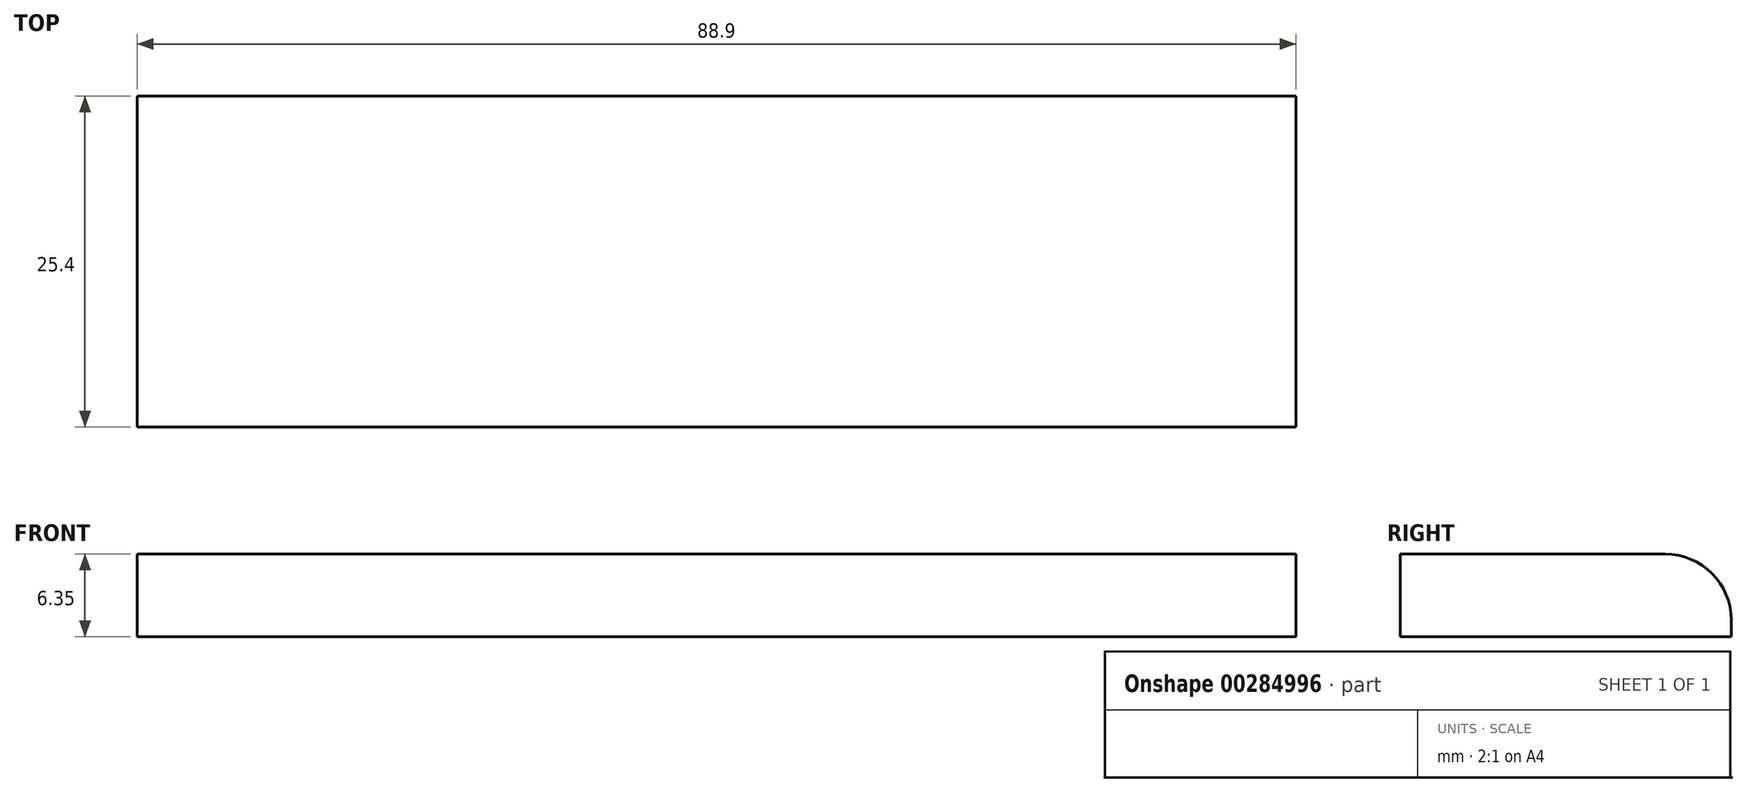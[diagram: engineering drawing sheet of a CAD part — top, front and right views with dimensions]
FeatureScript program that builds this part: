
annotation { "Feature Type Name" : "Feature", "Feature Type Description" : "" }
export const myFeature = defineFeature(function(context is Context, id is Id, definition is map)
    precondition{}
    {
        {
            var Q0;
            Q0=qCreatedBy(makeId("Top.planeOp"),FACE);
            var sketch = newSketch(context, id + "F0", { "sketchPlane" : qUnion([Q0])});
            skLineSegment(sketch, "E0.bottom", {"start": v(-19.7, -27.58) * mm, "end": v(-108.6, -27.58) * mm});
            skLineSegment(sketch, "E0.top", {"start": v(-19.7, -2.18) * mm, "end": v(-108.6, -2.18) * mm});
            skLineSegment(sketch, "E0.left", {"start": v(-19.7, -27.58) * mm, "end": v(-19.7, -2.18) * mm});
            skLineSegment(sketch, "E0.right", {"start": v(-108.6, -27.58) * mm, "end": v(-108.6, -2.18) * mm});
            skPoint(sketch, "E0.middle", {"position": v(-64.16, -14.88) * mm});
            skSolve(sketch);
        }
        {
            var Q0;
            Q0=makeQuery(id+"F0.imprint","IMPRINT",FACE,{"disambiguationData":[TD([[makeQuery(id+"F0.imprint","IMPRINT",EDGE,{"derivedFrom":sQuery(id+"F0.wireOp",EDGE,"E0.bottom")}),-1.0]])]});
            extrude(context, id + "F1", {"entities" : qUnion([Q0]), "depth" : 6.35 * mm});
        }
        {
            var Q0;
            Q0=makeQuery(id+"F1.opExtrude","CAP_EDGE",EDGE,{"disambiguationData":[OSD([sQuery(id+"F0.wireOp",EDGE,"E0.top")])],"isStart":false});
            fillet(context, id + "F2", {"entities" : qUnion([Q0]), "radius" : 5.08 * mm, "tangentPropagation" : true, "allowEdgeOverflow" : false});
        }
    });
